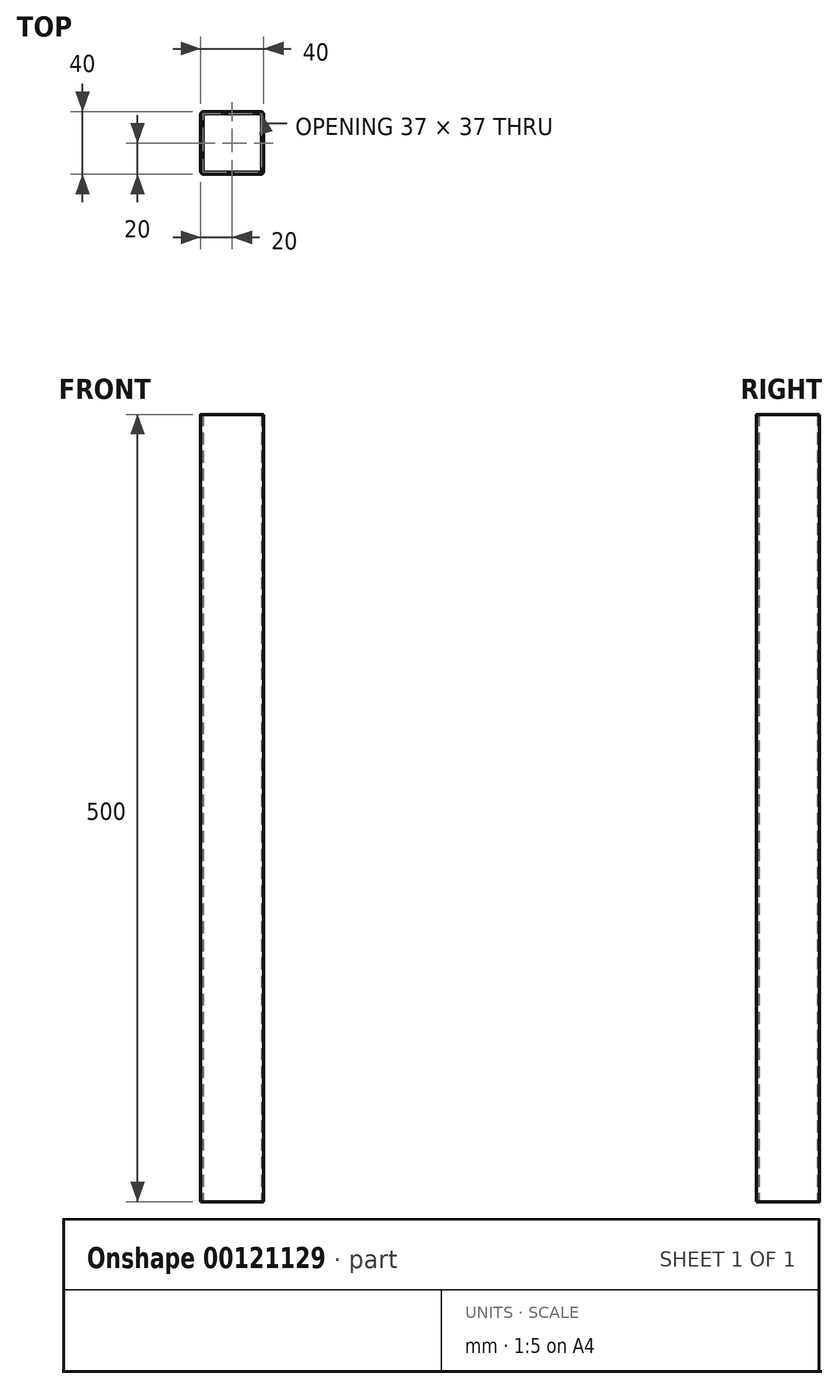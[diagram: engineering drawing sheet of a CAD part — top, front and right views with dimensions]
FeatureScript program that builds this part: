
annotation { "Feature Type Name" : "Feature", "Feature Type Description" : "" }
export const myFeature = defineFeature(function(context is Context, id is Id, definition is map)
    precondition{}
    {
        {
            var Q0;
            Q0=qCreatedBy(makeId("Top.planeOp"),FACE);
            var sketch = newSketch(context, id + "F0", { "sketchPlane" : qUnion([Q0])});
            skLineSegment(sketch, "E0.bottom", {"start": v(18, -20) * mm, "end": v(-18, -20) * mm});
            skLineSegment(sketch, "E0.top", {"start": v(18, 20) * mm, "end": v(-18, 20) * mm});
            skLineSegment(sketch, "E0.left", {"start": v(20, -18) * mm, "end": v(20, 18) * mm});
            skLineSegment(sketch, "E0.right", {"start": v(-20, -18) * mm, "end": v(-20, 18) * mm});
            skPoint(sketch, "E0.middle", {"position": v(0, 0) * mm});
            skPoint(sketch, "E1.visualSharp", {"position": v(-20, 20) * mm});
            skArc(sketch, "E1.filletArc", {"start": v(-18, 20) * mm, "mid": v(-19.41, 19.41) * mm, "end": v(-20, 18) * mm});
            skPoint(sketch, "E2.visualSharp", {"position": v(20, 20) * mm});
            skArc(sketch, "E2.filletArc", {"start": v(20, 18) * mm, "mid": v(19.41, 19.41) * mm, "end": v(18, 20) * mm});
            skPoint(sketch, "E3.visualSharp", {"position": v(20, -20) * mm});
            skArc(sketch, "E3.filletArc", {"start": v(18, -20) * mm, "mid": v(19.41, -19.41) * mm, "end": v(20, -18) * mm});
            skPoint(sketch, "E4.visualSharp", {"position": v(-20, -20) * mm});
            skArc(sketch, "E4.filletArc", {"start": v(-20, -18) * mm, "mid": v(-19.41, -19.41) * mm, "end": v(-18, -20) * mm});
            skPoint(sketch, "E5.visualSharp", {"position": v(-18.5, 18.5) * mm});
            skArc(sketch, "E6.0", {"start": v(18, -18.5) * mm, "mid": v(18.35, -18.35) * mm, "end": v(18.5, -18) * mm});
            skLineSegment(sketch, "E6.1", {"start": v(18.5, -18) * mm, "end": v(18.5, 18) * mm});
            skLineSegment(sketch, "E6.2", {"start": v(18, -18.5) * mm, "end": v(-18, -18.5) * mm});
            skArc(sketch, "E6.3", {"start": v(18.5, 18) * mm, "mid": v(18.35, 18.35) * mm, "end": v(18, 18.5) * mm});
            skArc(sketch, "E6.4", {"start": v(-18.5, -18) * mm, "mid": v(-18.35, -18.35) * mm, "end": v(-18, -18.5) * mm});
            skLineSegment(sketch, "E6.5", {"start": v(-18.5, -18) * mm, "end": v(-18.5, 18) * mm});
            skArc(sketch, "E6.6", {"start": v(-18, 18.5) * mm, "mid": v(-18.35, 18.35) * mm, "end": v(-18.5, 18) * mm});
            skLineSegment(sketch, "E6.7", {"start": v(18, 18.5) * mm, "end": v(-18, 18.5) * mm});
            skSolve(sketch);
        }
        {
            var Q0;
            Q0=makeQuery(id+"F0.imprint","IMPRINT",FACE,{"disambiguationData":[TD([[makeQuery(id+"F0.imprint","IMPRINT",EDGE,{"derivedFrom":sQuery(id+"F0.wireOp",EDGE,"E0.bottom")}),-1.0]])]});
            extrude(context, id + "F1", {"entities" : qUnion([Q0]), "depth" : 500 * mm});
        }
    });
